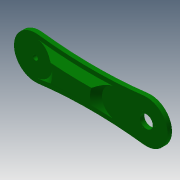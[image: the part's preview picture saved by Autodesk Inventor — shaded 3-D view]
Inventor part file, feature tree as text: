
AUTODESK INVENTOR PART (.ipt)
format: ipt  version: 2013 (Build 170138000, 138)  size: 307,712 bytes
history: native  units: mm
features: sketch x20, extrude x18, chamfer x1
ambient origin geometry x8: Origin, YZ Plane, XZ Plane, XY Plane, X Axis, Y Axis, Z Axis, Center Point
bodies: Solid1 (feature_tree)
feature tree (39):
  extrude  "Extrusion1"  Depth=50.0mm
  extrude  "Extrusion2"  Depth=6.0mm
  extrude  "Extrusion3"  Depth=5.0mm TaperAngle=0.0deg
  extrude  "Extrusion4"  Depth=20.0mm
  extrude  "Extrusion5"  Depth=20.0mm
  extrude  "Extrusion6"  Depth=3.0mm
  sketch  "Sketch7"  dims[d22=3.0mm d23=5.0mm d24=0.0mm]
  extrude  "Extrusion7"  Depth=5.0mm TaperAngle=0.0deg
  extrude  "Extrusion8"  Depth=1.0mm
  extrude  "Extrusion9"  Depth=1.0mm
  extrude  "Extrusion10"  Depth=15.0mm
  extrude  "Extrusion11"  Depth=5.0mm TaperAngle=0.0deg
  sketch  "Sketch12"  dims[d44=1.0mm d45=1.0mm]
  sketch  "Sketch13"  dims[d46=1.0mm d47=5.0mm d48=0.0mm]
  extrude  "Extrusion12"  Depth=1.0mm
  extrude  "Extrusion13"  Depth=5.0mm TaperAngle=0.0deg
  extrude  "Extrusion14"  Depth=5.0mm TaperAngle=0.0deg
  extrude  "Extrusion15"  Depth=5.0mm TaperAngle=0.0deg
  extrude  "Extrusion16"  Depth=43.308mm
  sketch  "Sketch18"  dims[d62=33.15mm d63=18.1mm]
  extrude  "Extrusion17"  Depth=20.0mm
  chamfer  "Chamfer1"  Distance=5.0mm
  extrude  "Extrusion18"  Depth=18.1mm
  sketch  "Sketch1"  dims[d0=150.0mm d1=50.0mm]
  sketch  "Sketch2"  dims[d2=5.0mm d3=0.0mm d4=6.0mm]
  sketch  "Sketch3"  dims[d5=6.0mm d6=5.0mm d7=0.0mm]
  sketch  "Sketch4"  dims[d11=55.0mm d12=20.0mm]
  sketch  "Sketch5"  dims[d13=40.2mm d14=20.0mm]
  sketch  "Sketch6"  dims[d20=3.0mm d21=3.0mm]
  sketch  "Sketch8"  dims[d32=5.0mm d33=0.0mm d34=1.0mm]
  sketch  "Sketch9"  dims[d35=1.0mm d36=1.0mm]
  sketch  "Sketch10"  dims[d37=5.0mm d38=0.0mm d39=15.0mm]
  sketch  "Sketch11"  dims[d40=15.0mm d41=5.0mm d42=0.0mm]
  sketch  "Sketch14"  dims[d49=5.0mm d50=0.0mm d51=5.0mm d52=0.0mm]
  sketch  "Sketch15"  dims[d53=130.0mm d54=5.0mm d55=0.0mm]
  sketch  "Sketch16"  dims[d56=15.0mm d57=43.308mm]
  sketch  "Sketch17"  dims[d58=40.2mm d59=20.0mm d60=5.0mm d61=0.0mm]
  sketch  "Sketch19"  dims[d64=55.0mm]
  sketch  "Sketch20"  dims[d65=40.2mm d66=20.0mm d67=5.0mm d68=0.0mm d69=33.15mm d70=18.1mm d71=55.0mm d72=40.2mm d73=20.0mm d74=5.0mm d75=0.0mm d76=5.0mm d77=0.0mm d84=5.0mm d85=0.0mm d86=5.0mm d87=0.0mm d95=7.0mm d96=0.0mm d97=7.0mm d98=2.0mm d99=45.0deg d100=6.0mm d101=5.0mm d102=0.0mm]
